# Revit family: Andreu World Uves Occasional
name_source: partatom
category: Mobiliario
revit_build: Autodesk Revit 2013 (Build: 20120221_2030(x64)
units: mm (PartAtom-declared; Revit-internal decimal feet)

## types (8) — shared parameters
Base = 340 mm  [stored 1.11549 ft]
Descripción = Occasional table.
Fabricante = Andreu World
Glides = Andreu World Plastic Glides
Modelo = Uves Occasional
Top Base = 500 mm  [stored 1.64042 ft]
Top Thickness = 30 mm  [stored 0.0984252 ft]
URL = http://www.andreuworld.com

## per-type parameters (varying)
| type | Height | Length | Referencia | Round Top | Square Top | Top | Top Diameter |
| ME-3696 Oak | 400 mm  [stored 1.31234 ft] | 550 mm  [stored 1.80446 ft] | ME-3696 | Sí | No | Andreu World Oak | 600 mm |
| ME-3700 Lacquered | 400 mm  [stored 1.31234 ft] | 663 mm | ME-3700 | Sí | No | Andreu World Lacquered | 600 mm |
| ME-3697 Oak | 500 mm  [stored 1.64042 ft] | 663 mm | ME-3697 | Sí | No | Andreu World Oak | 700 mm  [stored 2.29659 ft] |
| ME-3701 Lacquered | 500 mm  [stored 1.64042 ft] | 550 mm  [stored 1.80446 ft] | ME-3701 | Sí | No | Andreu World Lacquered | 700 mm  [stored 2.29659 ft] |
| ME-3698 Oak | 400 mm  [stored 1.31234 ft] | 550 mm  [stored 1.80446 ft] | ME-3698 | No | Sí | Andreu World Oak | 600 mm |
| ME-3702 Lacquered | 400 mm  [stored 1.31234 ft] | 550 mm  [stored 1.80446 ft] | ME-3702 | No | Sí | Andreu World Lacquered | 600 mm |
| ME-3699 Oak | 500 mm  [stored 1.64042 ft] | 600 mm | ME-3702 | No | Sí | Andreu World Oak | 600 mm |
| ME-3703 Lacquered | 500 mm  [stored 1.64042 ft] | 600 mm | ME-3702 | No | Sí | Andreu World Lacquered | 600 mm |

note: [stored X ft] marks values corroborated as IEEE doubles in the binary element streams (Revit-internal decimal feet)

## geometry (parser evidence)
native form markers: Blend x12
no freeform markers — native parametric forms only
